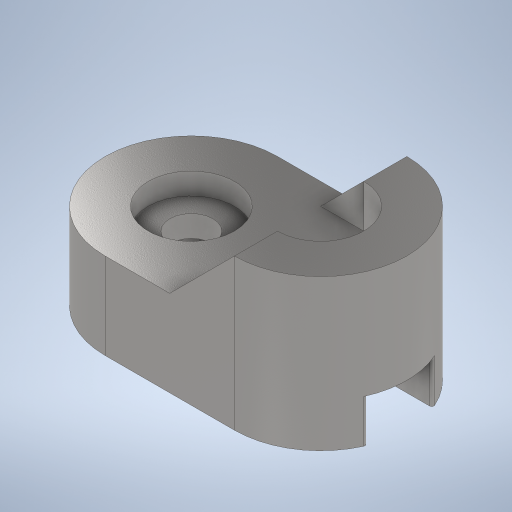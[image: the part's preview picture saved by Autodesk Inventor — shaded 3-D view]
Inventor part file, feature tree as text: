
AUTODESK INVENTOR PART (.ipt)
format: ipt  version: 2024 (Build 280153000, 153)  size: 356,864 bytes
history: native  units: mm
features: sketch x7, extrude x5, fillet x5, hole x2, plane x2, mirror x1
ambient origin geometry x8: Origin, YZ Plane, XZ Plane, XY Plane, X Axis, Y Axis, Z Axis, Center Point
bodies: Volumenkörper1 (feature_tree)
feature tree (22):
  extrude  "Extrusion1"  Depth=40.0mm
  fillet  "Rundung1"  Radius=40.0mm
  fillet  "Rundung2"  Radius=40.0mm
  fillet  "Rundung3"  Radius=40.0mm
  fillet  "Rundung4"  Radius=40.0mm
  extrude  "Extrusion2"  Depth=40.0mm
  hole  "Bohrung1"  [1 undecoded]
  hole  "Bohrung2"  [1 undecoded]
  extrude  "Extrusion3"  Depth=10.0mm TaperAngle=0.0deg
  extrude  "Extrusion4"  TaperAngle=0.0deg  [1 undecoded]
  plane  "Arbeitsebene1"
  mirror  "Spiegeln2"
  plane  "Arbeitsebene3"
  extrude  "Extrusion5"  TaperAngle=0.0deg  [1 undecoded]
  fillet  "Rundung5"  Radius=30.0mm
  sketch  "Skizze1"  dims[d0=80.0mm d1=140.0mm d2=40.0mm d3=0.0mm d5=40.0mm d6=40.0mm d7=40.0mm]
  sketch  "Skizze4"  dims[d8=40.0mm d10=40.0mm]
  sketch  "Skizze5"  dims[d11=40.0mm d12=60.0mm]
  sketch  "Skizze6"  dims[d13=10.0mm d14=0.0mm]
  sketch  "Skizze7"  dims[d15=20.0mm d16=6.0mm d17=4.0mm d18=2.0mm d19=90.0deg d20=72.0mm d21=0.0mm]
  sketch  "Skizze8"  dims[d22=20.0mm d23=6.0mm d24=4.0mm d25=2.0mm d26=90.0deg d27=8.0mm d28=0.0mm d29=30.0mm d30=0.0mm]
  sketch  "Skizze10"  dims[d31=30.0mm d32=10.0mm d33=0.0mm d34=0.0mm d35=0.0mm d36=30.0mm d37=20.0mm d38=0.0mm d39=0.0mm d40=1.0mm]
note: 4 required parameter values undecoded (feature->parameter linkage not recoverable at this tier; creation-order binding heuristic only, values carry confidence <= 0.55)
